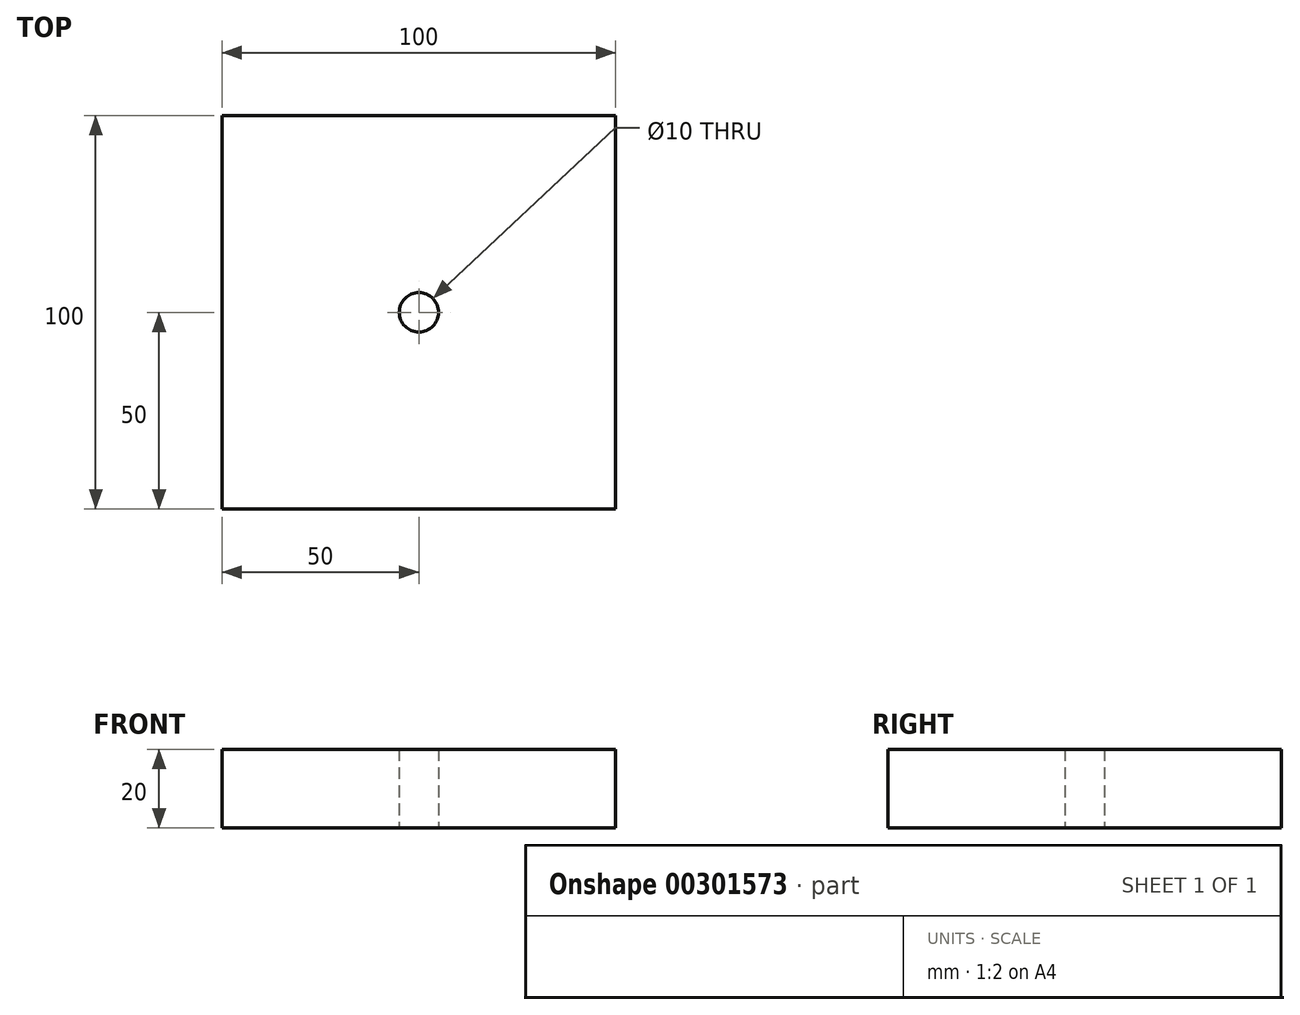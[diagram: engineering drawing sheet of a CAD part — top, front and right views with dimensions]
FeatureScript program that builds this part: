
annotation { "Feature Type Name" : "Feature", "Feature Type Description" : "" }
export const myFeature = defineFeature(function(context is Context, id is Id, definition is map)
    precondition{}
    {
        {
            var Q0;
            Q0=qCreatedBy(makeId("Top.planeOp"),FACE);
            var sketch = newSketch(context, id + "F0", { "sketchPlane" : qUnion([Q0])});
            skLineSegment(sketch, "E0.bottom", {"start": v(0, 0) * mm, "end": v(100, 0) * mm});
            skLineSegment(sketch, "E0.top", {"start": v(0, 100) * mm, "end": v(100, 100) * mm});
            skLineSegment(sketch, "E0.left", {"start": v(0, 0) * mm, "end": v(0, 100) * mm});
            skLineSegment(sketch, "E0.right", {"start": v(100, 0) * mm, "end": v(100, 100) * mm});
            skCircle(sketch, "E1", {"center": v(50, 50) * mm, "radius": 5 * mm});
            skPoint(sketch, "E1.centerSnap0", {"position": v(50, 0) * mm});
            skPoint(sketch, "E1.centerSnap1", {"position": v(0, 50) * mm});
            skSolve(sketch);
        }
        {
            var Q0;
            Q0 = qSketchRegion(id + "F0", true);
            extrude(context, id + "F1", {"entities" : qUnion([Q0]), "depth" : 20 * mm});
        }
    });
